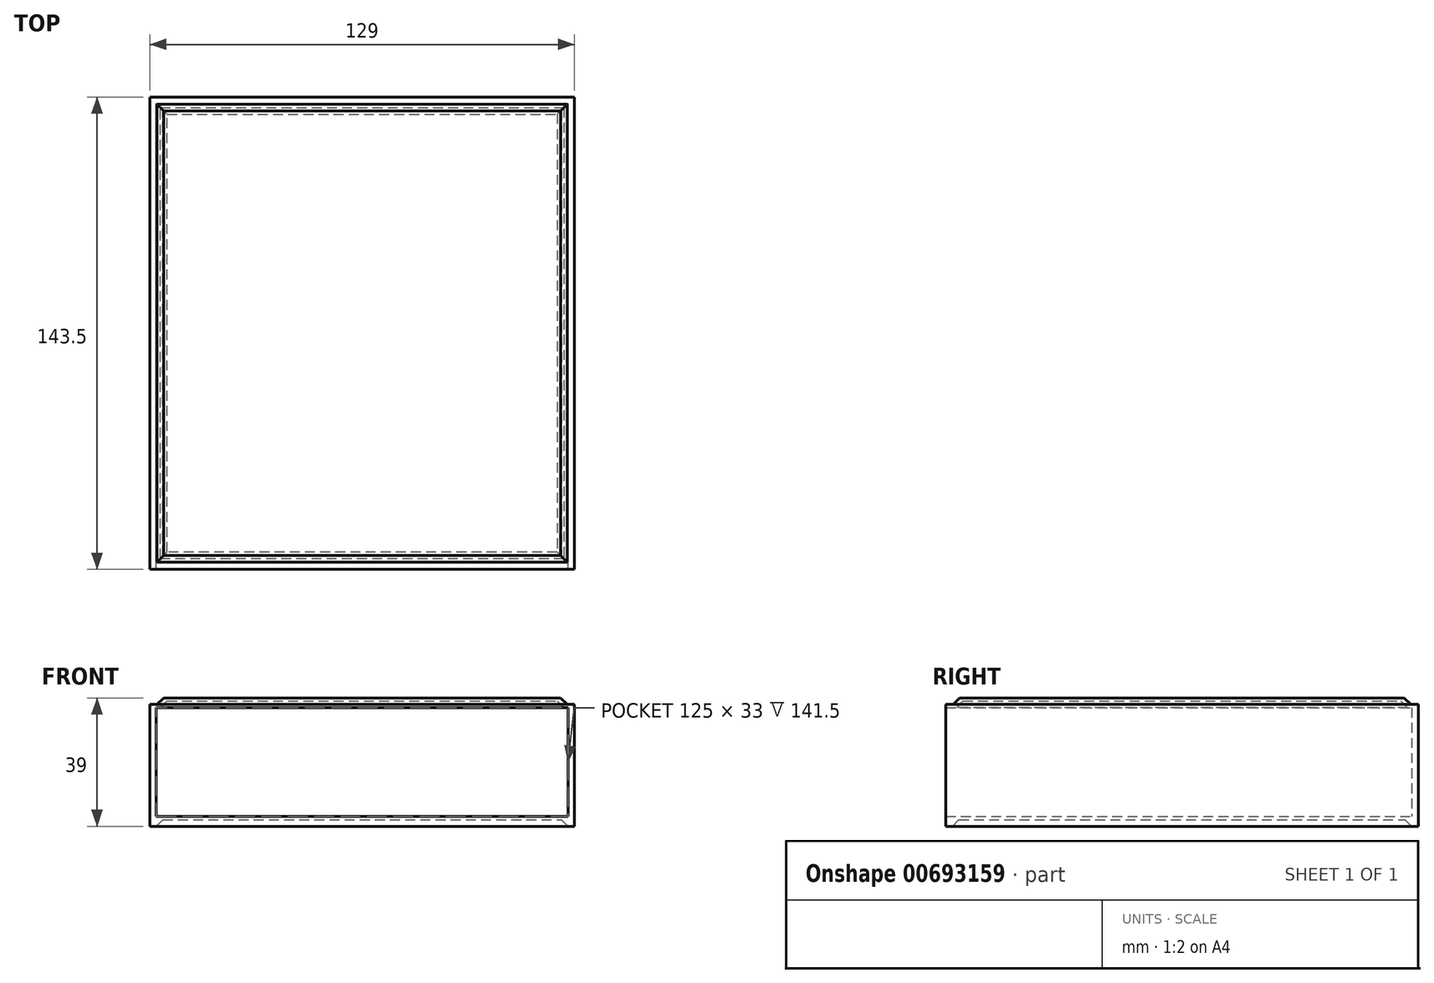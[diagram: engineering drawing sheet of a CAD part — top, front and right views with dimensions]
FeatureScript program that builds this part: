
annotation { "Feature Type Name" : "Feature", "Feature Type Description" : "" }
export const myFeature = defineFeature(function(context is Context, id is Id, definition is map)
    precondition{}
    {
        {
            var Q0;
            Q0=qCreatedBy(makeId("Top.planeOp"),FACE);
            var sketch = newSketch(context, id + "F0", { "sketchPlane" : qUnion([Q0])});
            skLineSegment(sketch, "E0.bottom", {"start": v(64.5, -71.75) * mm, "end": v(-64.5, -71.75) * mm});
            skLineSegment(sketch, "E0.top", {"start": v(64.5, 71.75) * mm, "end": v(-64.5, 71.75) * mm});
            skLineSegment(sketch, "E0.left", {"start": v(64.5, -71.75) * mm, "end": v(64.5, 71.75) * mm});
            skLineSegment(sketch, "E0.right", {"start": v(-64.5, -71.75) * mm, "end": v(-64.5, 71.75) * mm});
            skPoint(sketch, "E0.middle", {"position": v(0, 0) * mm});
            skLineSegment(sketch, "E1.bottom", {"start": v(62.5, -69.75) * mm, "end": v(-62.5, -69.75) * mm});
            skLineSegment(sketch, "E1.top", {"start": v(62.5, 69.75) * mm, "end": v(-62.5, 69.75) * mm});
            skLineSegment(sketch, "E1.left", {"start": v(62.5, -69.75) * mm, "end": v(62.5, 69.75) * mm});
            skLineSegment(sketch, "E1.right", {"start": v(-62.5, -69.75) * mm, "end": v(-62.5, 69.75) * mm});
            skSolve(sketch);
        }
        {
            var Q0;
            Q0=makeQuery(id+"F0.imprint","IMPRINT",FACE,{"disambiguationData":[TD([[makeQuery(id+"F0.imprint","IMPRINT",EDGE,{"derivedFrom":sQuery(id+"F0.wireOp",EDGE,"E0.bottom")}),-1.0]])]});
            var Q1;
            Q1=makeQuery(id+"F0.imprint","IMPRINT",FACE,{"disambiguationData":[TD([[makeQuery(id+"F0.imprint","IMPRINT",EDGE,{"derivedFrom":sQuery(id+"F0.wireOp",EDGE,"E1.bottom")}),-1.0]])]});
            extrude(context, id + "F1", {"entities" : qUnion([Q0, Q1]), "depth" : 3 * mm, "offsetDistance" : 25 * mm});
        }
        {
            var Q0;
            Q0=makeQuery(id+"F0.imprint","IMPRINT",FACE,{"disambiguationData":[TD([[makeQuery(id+"F0.imprint","IMPRINT",EDGE,{"derivedFrom":sQuery(id+"F0.wireOp",EDGE,"E1.bottom")}),-1.0]])]});
            extrude(context, id + "F2", {"entities" : qUnion([Q0]), "operationType" : NewBodyOperationType.REMOVE, "depth" : 2 * mm, "offsetDistance" : 25 * mm});
        }
        {
            var Q0;
            Q0=makeQuery(id+"F2.boolean.opBoolean","COPY",FACE,{"derivedFrom":makeQuery(id+"F2.opExtrude","CAP_FACE",FACE,{"disambiguationData":[OSD([sQuery(id+"F0.wireOp",EDGE,"E1.bottom"),sQuery(id+"F0.wireOp",EDGE,"E1.top"),sQuery(id+"F0.wireOp",EDGE,"E1.left"),sQuery(id+"F0.wireOp",EDGE,"E1.right")])],"isStart":false})});
            chamfer(context, id + "F3", {"entities" : qUnion([Q0]), "width" : 2 * mm, "tangentPropagation" : true});
        }
        {
            var Q0;
            Q0=makeQuery(id+"F1.opExtrude","CAP_FACE",FACE,{"disambiguationData":[OSD([sQuery(id+"F0.wireOp",EDGE,"E0.bottom"),sQuery(id+"F0.wireOp",EDGE,"E0.top"),sQuery(id+"F0.wireOp",EDGE,"E0.left"),sQuery(id+"F0.wireOp",EDGE,"E0.right")])],"isStart":false});
            var sketch = newSketch(context, id + "F4", { "sketchPlane" : qUnion([Q0])});
            skLineSegment(sketch, "E2.bottom", {"start": v(-64.5, -71.75) * mm, "end": v(64.5, -71.75) * mm});
            skLineSegment(sketch, "E2.top", {"start": v(-64.5, 71.75) * mm, "end": v(64.5, 71.75) * mm});
            skLineSegment(sketch, "E2.left", {"start": v(-64.5, -71.75) * mm, "end": v(-64.5, 71.75) * mm});
            skLineSegment(sketch, "E2.right", {"start": v(64.5, -71.75) * mm, "end": v(64.5, 71.75) * mm});
            skLineSegment(sketch, "E3.bottom", {"start": v(-62.5, -71.75) * mm, "end": v(62.5, -71.75) * mm});
            skLineSegment(sketch, "E3.top", {"start": v(-62.5, 69.75) * mm, "end": v(62.5, 69.75) * mm});
            skLineSegment(sketch, "E3.left", {"start": v(-62.5, -71.75) * mm, "end": v(-62.5, 69.75) * mm});
            skLineSegment(sketch, "E3.right", {"start": v(62.5, -71.75) * mm, "end": v(62.5, 69.75) * mm});
            skSolve(sketch);
        }
        {
            var Q0;
            Q0=makeQuery(id+"F4.imprint","IMPRINT",FACE,{"disambiguationData":[TD([[makeQuery(id+"F4.imprint","IMPRINT",EDGE,{"derivedFrom":sQuery(id+"F4.wireOp",EDGE,"E2.top")}),1.0]])]});
            extrude(context, id + "F5", {"entities" : qUnion([Q0]), "operationType" : NewBodyOperationType.ADD, "depth" : 33 * mm, "offsetDistance" : 25 * mm});
        }
        {
            var Q0;
            Q0=makeQuery(id+"F5.opExtrude","CAP_FACE",FACE,{"disambiguationData":[OSD([sQuery(id+"F4.wireOp",EDGE,"E2.bottom"),sQuery(id+"F4.wireOp",EDGE,"E2.top"),sQuery(id+"F4.wireOp",EDGE,"E2.left"),sQuery(id+"F4.wireOp",EDGE,"E2.right"),sQuery(id+"F4.wireOp",EDGE,"E3.top"),sQuery(id+"F4.wireOp",EDGE,"E3.left"),sQuery(id+"F4.wireOp",EDGE,"E3.right")])],"isStart":false});
            var sketch = newSketch(context, id + "F6", { "sketchPlane" : qUnion([Q0])});
            skLineSegment(sketch, "E4.bottom", {"start": v(-64.5, -71.75) * mm, "end": v(64.5, -71.75) * mm});
            skLineSegment(sketch, "E4.top", {"start": v(-64.5, 71.75) * mm, "end": v(64.5, 71.75) * mm});
            skLineSegment(sketch, "E4.left", {"start": v(-64.5, -71.75) * mm, "end": v(-64.5, 71.75) * mm});
            skLineSegment(sketch, "E4.right", {"start": v(64.5, -71.75) * mm, "end": v(64.5, 71.75) * mm});
            skLineSegment(sketch, "E5.bottom", {"start": v(-62.25, 69.5) * mm, "end": v(62.25, 69.5) * mm});
            skLineSegment(sketch, "E5.top", {"start": v(-62.25, -69.5) * mm, "end": v(62.25, -69.5) * mm});
            skLineSegment(sketch, "E5.left", {"start": v(-62.25, 69.5) * mm, "end": v(-62.25, -69.5) * mm});
            skLineSegment(sketch, "E5.right", {"start": v(62.25, 69.5) * mm, "end": v(62.25, -69.5) * mm});
            skLineSegment(sketch, "E6.bottom", {"start": v(-61.25, 68.5) * mm, "end": v(61.25, 68.5) * mm});
            skLineSegment(sketch, "E6.top", {"start": v(-61.25, -68.5) * mm, "end": v(61.25, -68.5) * mm});
            skLineSegment(sketch, "E6.left", {"start": v(-61.25, 68.5) * mm, "end": v(-61.25, -68.5) * mm});
            skLineSegment(sketch, "E6.right", {"start": v(61.25, 68.5) * mm, "end": v(61.25, -68.5) * mm});
            skSolve(sketch);
        }
        {
            var Q0;
            Q0=makeQuery(id+"F6.imprint","IMPRINT",FACE,{"disambiguationData":[TD([[makeQuery(id+"F6.imprint","IMPRINT",EDGE,{"derivedFrom":sQuery(id+"F6.wireOp",EDGE,"E5.bottom")}),1.0]])]});
            var Q1;
            Q1=makeQuery(id+"F6.imprint","IMPRINT",FACE,{"disambiguationData":[TD([[makeQuery(id+"F6.imprint","IMPRINT",EDGE,{"derivedFrom":sQuery(id+"F6.wireOp",EDGE,"E5.bottom")}),-1.0]])]});
            var Q2;
            Q2=makeQuery(id+"F6.imprint","IMPRINT",FACE,{"disambiguationData":[TD([[makeQuery(id+"F6.imprint","IMPRINT",EDGE,{"derivedFrom":sQuery(id+"F6.wireOp",EDGE,"E4.top")}),1.0]])]});
            extrude(context, id + "F7", {"entities" : qUnion([Q0, Q1, Q2]), "operationType" : NewBodyOperationType.ADD, "depth" : 1 * mm, "offsetDistance" : 25 * mm});
        }
        {
            var Q0;
            {var subQ0=sQuery(id+"F6.wireOp",EDGE,"d14ea8a3-13da-46dc-b887-d83dcd02b8a7.bottom");Q0=makeQuery(id+"F6.imprint","IMPRINT",FACE,{"disambiguationData":[TD([[makeQuery(id+"F6.imprint","IMPRINT",EDGE,{"derivedFrom":subQ0}),1.0]])]});}
            var Q1;
            Q1=makeQuery(id+"F6.imprint","IMPRINT",FACE,{"disambiguationData":[TD([[makeQuery(id+"F6.imprint","IMPRINT",EDGE,{"derivedFrom":sQuery(id+"F6.wireOp",EDGE,"E5.bottom")}),-1.0]])]});
            var Q2;
            Q2=makeQuery(id+"F6.imprint","IMPRINT",FACE,{"disambiguationData":[TD([[makeQuery(id+"F6.imprint","IMPRINT",EDGE,{"derivedFrom":sQuery(id+"F6.wireOp",EDGE,"E6.bottom")}),-1.0]])]});
            extrude(context, id + "F8", {"entities" : qUnion([Q0, Q1, Q2]), "operationType" : NewBodyOperationType.ADD, "depth" : 3 * mm, "offsetDistance" : 25 * mm});
        }
        {
            var Q0;
            Q0=makeQuery(id+"F8.opExtrude","CAP_EDGE",EDGE,{"disambiguationData":[OSD([sQuery(id+"F6.wireOp",EDGE,"d14ea8a3-13da-46dc-b887-d83dcd02b8a7.bottom")])],"isStart":false});
            var Q1;
            Q1=makeQuery(id+"F8.opExtrude","CAP_EDGE",EDGE,{"disambiguationData":[OSD([sQuery(id+"F4.wireOp",EDGE,"E3.left")])],"isStart":false});
            var Q2;
            Q2=makeQuery(id+"F8.opExtrude","CAP_EDGE",EDGE,{"disambiguationData":[OSD([sQuery(id+"F6.wireOp",EDGE,"d14ea8a3-13da-46dc-b887-d83dcd02b8a7.right")])],"isStart":false});
            var Q3;
            Q3=makeQuery(id+"F8.opExtrude","CAP_EDGE",EDGE,{"disambiguationData":[OSD([sQuery(id+"F6.wireOp",EDGE,"d14ea8a3-13da-46dc-b887-d83dcd02b8a7.top")])],"isStart":false});
            var Q4;
            Q4=makeQuery(id+"F8.opExtrude","CAP_FACE",FACE,{"disambiguationData":[OSD([sQuery(id+"F6.wireOp",EDGE,"E5.bottom"),sQuery(id+"F6.wireOp",EDGE,"E5.top"),sQuery(id+"F6.wireOp",EDGE,"E5.left"),sQuery(id+"F6.wireOp",EDGE,"E5.right")])],"isStart":false});
            chamfer(context, id + "F9", {"entities" : qUnion([Q0, Q1, Q2, Q3, Q4]), "width" : 2 * mm, "tangentPropagation" : true});
        }
        {
            var Q0;
            Q0=makeQuery(id+"F6.imprint","IMPRINT",FACE,{"disambiguationData":[TD([[makeQuery(id+"F6.imprint","IMPRINT",EDGE,{"derivedFrom":sQuery(id+"F6.wireOp",EDGE,"E6.bottom")}),-1.0]])]});
            extrude(context, id + "F10", {"entities" : qUnion([Q0]), "operationType" : NewBodyOperationType.REMOVE, "depth" : 2 * mm, "offsetDistance" : 25 * mm, "hasDraft" : true, "draftAngle" : 45 * degree, "draftPullDirection" : true});
        }
    });
